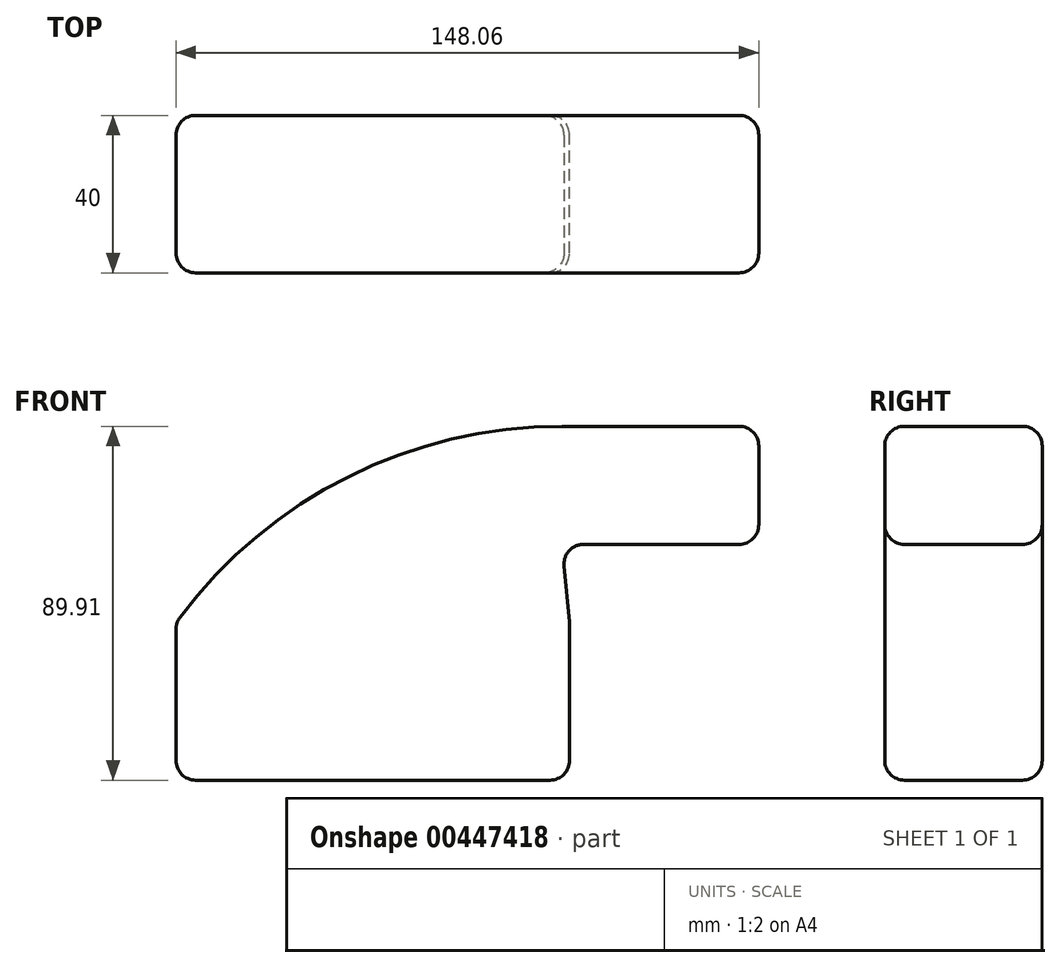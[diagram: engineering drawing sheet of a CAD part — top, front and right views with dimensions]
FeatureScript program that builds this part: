
annotation { "Feature Type Name" : "Feature", "Feature Type Description" : "" }
export const myFeature = defineFeature(function(context is Context, id is Id, definition is map)
    precondition{}
    {
        {
            var Q0;
            Q0=qCreatedBy(makeId("Front.planeOp"),FACE);
            var sketch = newSketch(context, id + "F0", { "sketchPlane" : qUnion([Q0])});
            skLineSegment(sketch, "E0.bottom", {"start": v(-50, -20) * mm, "end": v(50, -20) * mm});
            skLineSegment(sketch, "E0.top", {"start": v(-50, 20) * mm, "end": v(50, 20) * mm});
            skLineSegment(sketch, "E0.left", {"start": v(-50, -20) * mm, "end": v(-50, 20) * mm});
            skLineSegment(sketch, "E0.right", {"start": v(50, -20) * mm, "end": v(50, 20) * mm});
            skPoint(sketch, "E0.middle", {"position": v(0, 0) * mm});
            skLineSegment(sketch, "E1.bottom", {"start": v(98.06, 39.9) * mm, "end": v(48.06, 39.9) * mm});
            skLineSegment(sketch, "E1.top", {"start": v(98.06, 69.9) * mm, "end": v(48.06, 69.9) * mm});
            skLineSegment(sketch, "E1.left", {"start": v(98.06, 39.9) * mm, "end": v(98.06, 69.9) * mm});
            skLineSegment(sketch, "E1.right", {"start": v(48.06, 39.9) * mm, "end": v(48.06, 69.9) * mm});
            skPoint(sketch, "E1.middle", {"position": v(73.06, 54.9) * mm});
            skArc(sketch, "E2", {"start": v(48.06, 69.9) * mm, "mid": v(-6.96, 56.71) * mm, "end": v(-50, 20) * mm});
            skLineSegment(sketch, "E3", {"start": v(48.06, 39.9) * mm, "end": v(50, 20) * mm});
            skSolve(sketch);
        }
        {
            var Q0;
            Q0=makeQuery(id+"F0.imprint","IMPRINT",FACE,{"disambiguationData":[TD([[makeQuery(id+"F0.imprint","IMPRINT",EDGE,{"derivedFrom":sQuery(id+"F0.wireOp",EDGE,"E0.bottom")}),1.0]])]});
            var Q1;
            Q1=makeQuery(id+"F0.imprint","IMPRINT",FACE,{"disambiguationData":[TD([[makeQuery(id+"F0.imprint","IMPRINT",EDGE,{"derivedFrom":sQuery(id+"F0.wireOp",EDGE,"E0.top")}),1.0]])]});
            var Q2;
            Q2=makeQuery(id+"F0.imprint","IMPRINT",FACE,{"disambiguationData":[TD([[makeQuery(id+"F0.imprint","IMPRINT",EDGE,{"derivedFrom":sQuery(id+"F0.wireOp",EDGE,"E1.bottom")}),-1.0]])]});
            extrude(context, id + "F1", {"entities" : qUnion([Q0, Q1, Q2]), "depth" : 40 * mm});
        }
        {
            var Q0;
            Q0=makeQuery(id+"F1.opExtrude","CAP_EDGE",EDGE,{"disambiguationData":[OSD([sQuery(id+"F0.wireOp",EDGE,"E2")])],"isStart":true});
            var Q1;
            Q1=makeQuery(id+"F1.opExtrude","CAP_EDGE",EDGE,{"disambiguationData":[OSD([sQuery(id+"F0.wireOp",EDGE,"E3")])],"isStart":true});
            var Q2;
            Q2=makeQuery(id+"F1.opExtrude","CAP_EDGE",EDGE,{"disambiguationData":[OSD([sQuery(id+"F0.wireOp",EDGE,"E0.left")])],"isStart":false});
            var Q3;
            Q3=makeQuery(id+"F1.opExtrude","CAP_EDGE",EDGE,{"disambiguationData":[OSD([sQuery(id+"F0.wireOp",EDGE,"E0.right")])],"isStart":false});
            var Q4;
            Q4=makeQuery(id+"F1.opExtrude","CAP_EDGE",EDGE,{"disambiguationData":[OSD([sQuery(id+"F0.wireOp",EDGE,"E1.top")])],"isStart":false});
            var Q5;
            Q5=makeQuery(id+"F1.opExtrude","SWEPT_EDGE",EDGE,{"disambiguationData":[OSD([sQuery(id+"F0.wireOp",EDGE,"E0.bottom"),sQuery(id+"F0.wireOp",EDGE,"E0.right")])]});
            var Q6;
            Q6=makeQuery(id+"F1.opExtrude","CAP_EDGE",EDGE,{"disambiguationData":[OSD([sQuery(id+"F0.wireOp",EDGE,"E0.bottom")])],"isStart":false});
            var Q7;
            Q7=makeQuery(id+"F1.opExtrude","SWEPT_EDGE",EDGE,{"disambiguationData":[OSD([sQuery(id+"F0.wireOp",EDGE,"E1.top"),sQuery(id+"F0.wireOp",EDGE,"E1.right"),sQuery(id+"F0.wireOp",EDGE,"E2")])]});
            var Q8;
            Q8=makeQuery(id+"F1.opExtrude","CAP_EDGE",EDGE,{"disambiguationData":[OSD([sQuery(id+"F0.wireOp",EDGE,"E1.bottom")])],"isStart":false});
            var Q9;
            Q9=makeQuery(id+"F1.opExtrude","CAP_EDGE",EDGE,{"disambiguationData":[OSD([sQuery(id+"F0.wireOp",EDGE,"E0.right")])],"isStart":true});
            var Q10;
            Q10=makeQuery(id+"F1.opExtrude","CAP_EDGE",EDGE,{"disambiguationData":[OSD([sQuery(id+"F0.wireOp",EDGE,"E1.top")])],"isStart":true});
            var Q11;
            Q11=makeQuery(id+"F1.opExtrude","CAP_EDGE",EDGE,{"disambiguationData":[OSD([sQuery(id+"F0.wireOp",EDGE,"E2")])],"isStart":false});
            var Q12;
            Q12=makeQuery(id+"F1.opExtrude","SWEPT_EDGE",EDGE,{"disambiguationData":[OSD([sQuery(id+"F0.wireOp",EDGE,"E0.top"),sQuery(id+"F0.wireOp",EDGE,"E0.right"),sQuery(id+"F0.wireOp",EDGE,"E3")])]});
            var Q13;
            Q13=makeQuery(id+"F1.opExtrude","CAP_EDGE",EDGE,{"disambiguationData":[OSD([sQuery(id+"F0.wireOp",EDGE,"E3")])],"isStart":false});
            var Q14;
            Q14=makeQuery(id+"F1.opExtrude","CAP_EDGE",EDGE,{"disambiguationData":[OSD([sQuery(id+"F0.wireOp",EDGE,"E0.left")])],"isStart":true});
            var Q15;
            Q15=makeQuery(id+"F1.opExtrude","CAP_EDGE",EDGE,{"disambiguationData":[OSD([sQuery(id+"F0.wireOp",EDGE,"E0.bottom")])],"isStart":true});
            var Q16;
            Q16=makeQuery(id+"F1.opExtrude","SWEPT_EDGE",EDGE,{"disambiguationData":[OSD([sQuery(id+"F0.wireOp",EDGE,"E1.bottom"),sQuery(id+"F0.wireOp",EDGE,"E1.right"),sQuery(id+"F0.wireOp",EDGE,"E3")])]});
            var Q17;
            Q17=makeQuery(id+"F1.opExtrude","SWEPT_EDGE",EDGE,{"disambiguationData":[OSD([sQuery(id+"F0.wireOp",EDGE,"E0.bottom"),sQuery(id+"F0.wireOp",EDGE,"E0.left")])]});
            var Q18;
            Q18=makeQuery(id+"F1.opExtrude","CAP_EDGE",EDGE,{"disambiguationData":[OSD([sQuery(id+"F0.wireOp",EDGE,"E1.bottom")])],"isStart":true});
            var Q19;
            Q19=makeQuery(id+"F1.opExtrude","SWEPT_EDGE",EDGE,{"disambiguationData":[OSD([sQuery(id+"F0.wireOp",EDGE,"E0.top"),sQuery(id+"F0.wireOp",EDGE,"E0.left"),sQuery(id+"F0.wireOp",EDGE,"E2")])]});
            var Q20;
            Q20=makeQuery(id+"F1.opExtrude","SWEPT_FACE",FACE,{"disambiguationData":[OSD([sQuery(id+"F0.wireOp",EDGE,"E1.left")])]});
            fillet(context, id + "F2", {"entities" : qUnion([Q0, Q1, Q2, Q3, Q4, Q5, Q6, Q7, Q8, Q9, Q10, Q11, Q12, Q13, Q14, Q15, Q16, Q17, Q18, Q19, Q20]), "radius" : 5 * mm, "tangentPropagation" : true, "allowEdgeOverflow" : false});
        }
    });
